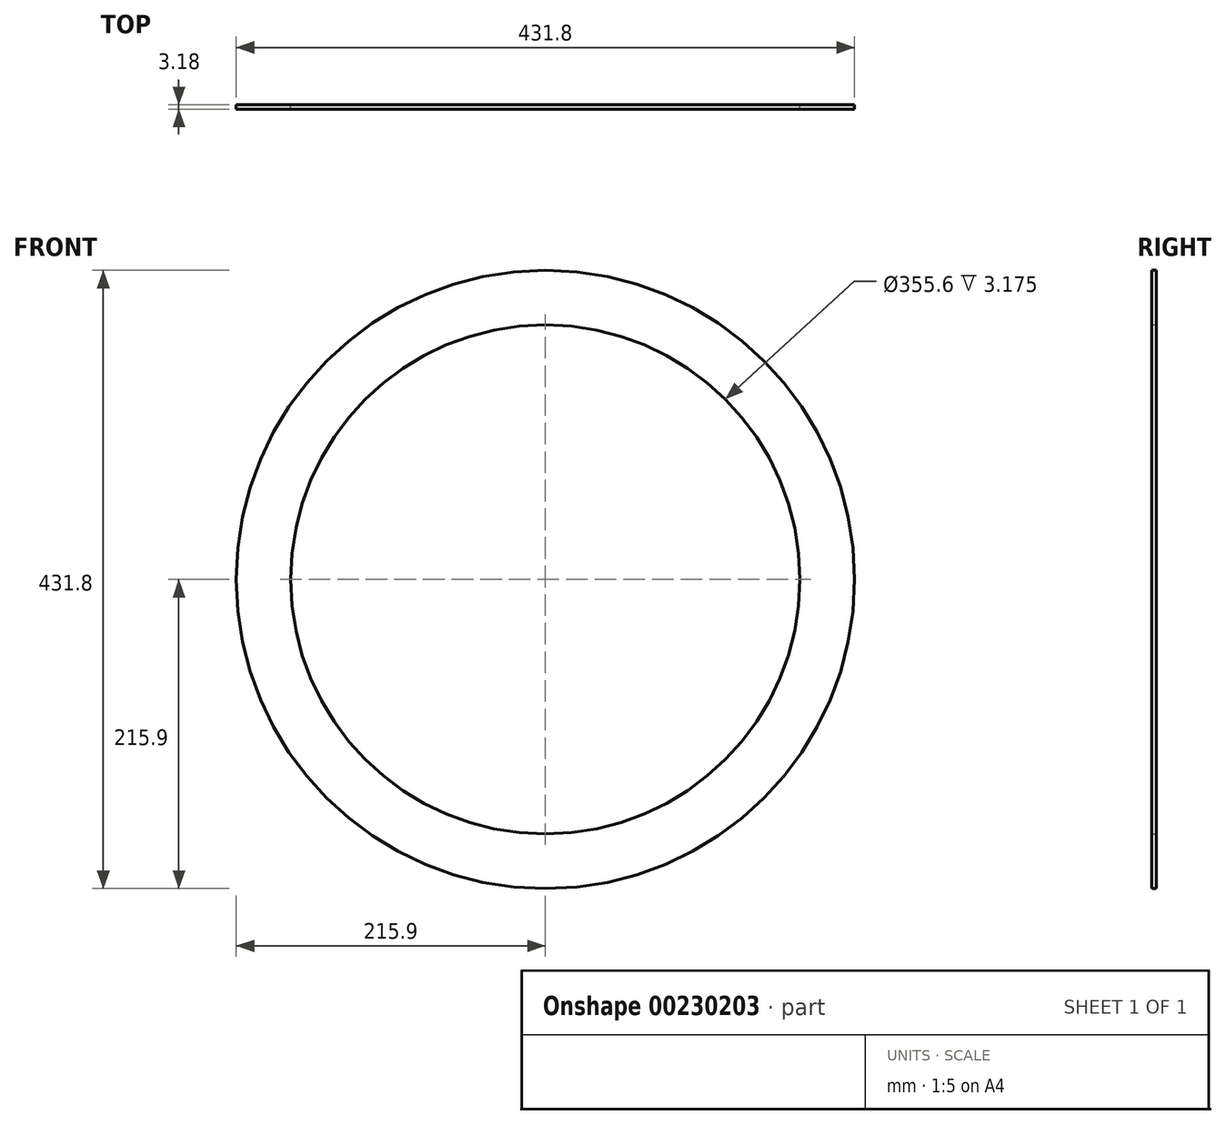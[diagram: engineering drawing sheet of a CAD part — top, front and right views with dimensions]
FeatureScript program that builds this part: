
annotation { "Feature Type Name" : "Feature", "Feature Type Description" : "" }
export const myFeature = defineFeature(function(context is Context, id is Id, definition is map)
    precondition{}
    {
        {
            var Q0;
            Q0=qCreatedBy(makeId("Front.planeOp"),FACE);
            var sketch = newSketch(context, id + "F0", { "sketchPlane" : qUnion([Q0])});
            skCircle(sketch, "E0", {"center": v(0, 0) * mm, "radius": 177.8 * mm});
            skCircle(sketch, "E1", {"center": v(0, 0) * mm, "radius": 215.9 * mm});
            skSolve(sketch);
        }
        {
            var Q0;
            Q0 = qSketchRegion(id + "F0", true);
            extrude(context, id + "F1", {"entities" : qUnion([Q0]), "depth" : 3.17 * mm});
        }
    });
